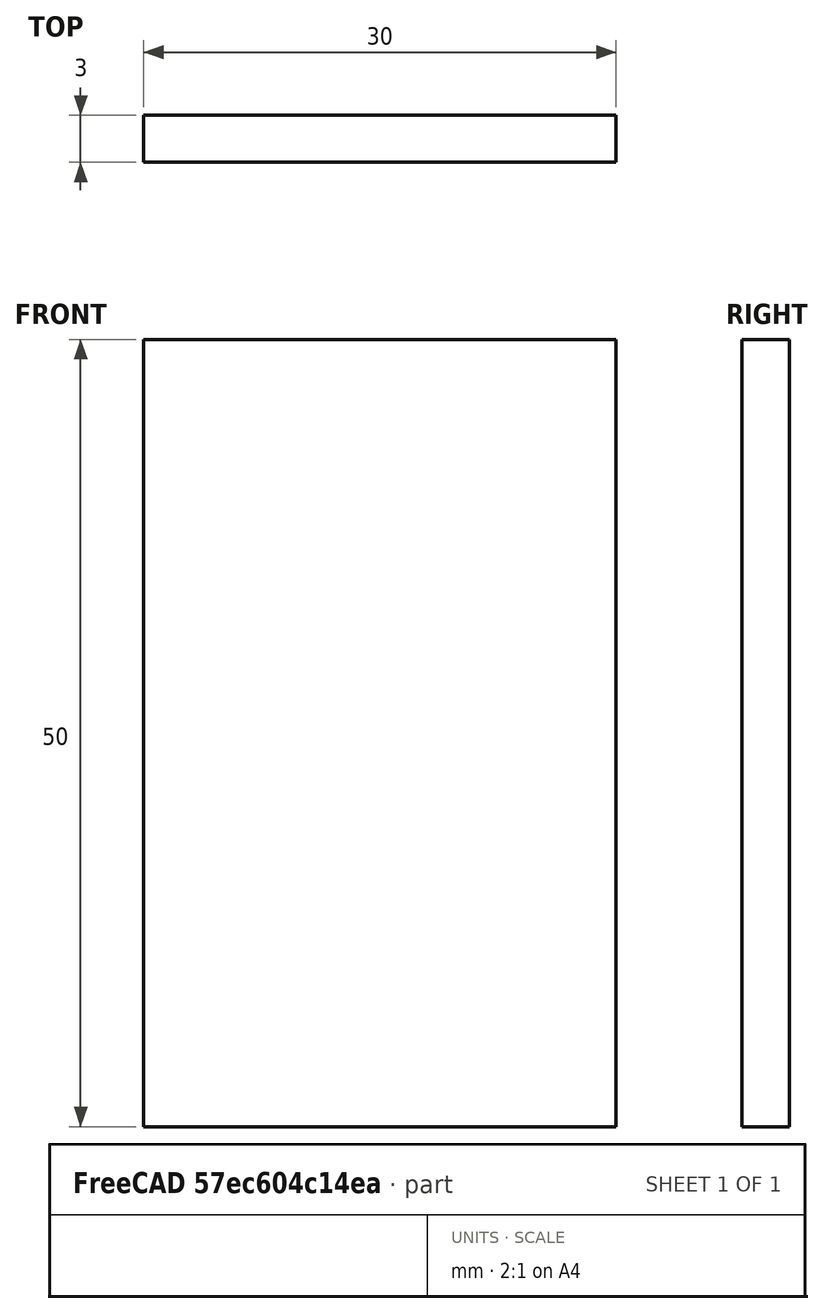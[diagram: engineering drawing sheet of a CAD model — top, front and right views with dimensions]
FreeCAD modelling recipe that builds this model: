
FCSTD DOCUMENT  (FreeCAD 0.15R4671 (Git))
Label: Flat Bar 30x3 EN10058 S235JR
License: All rights reserved
LicenseURL: http://en.wikipedia.org/wiki/All_rights_reserved
objects: Sketcher::SketchObject×1, Part::Extrusion×1
note: 2 computed .brp shape members not serialized (recipe doc carries the construction recipe); baked Part::Feature solids carry a one-line shape summary decoded from their .brp

FEATURE [Sketcher::SketchObject] Sketch
  sketch-geometry (4):
    g0: LineSegment StartX=-15 StartY=-1.5 StartZ=0 EndX=15 EndY=-1.5 EndZ=0
    g1: LineSegment StartX=15 StartY=-1.5 StartZ=0 EndX=15 EndY=1.5 EndZ=0
    g2: LineSegment StartX=15 StartY=1.5 StartZ=0 EndX=-15 EndY=1.5 EndZ=0
    g3: LineSegment StartX=-15 StartY=1.5 StartZ=0 EndX=-15 EndY=-1.5 EndZ=0
  constraints (12):
    c: Coincident(g0,g1)
    c: Coincident(g1,g2)
    c: Coincident(g2,g3)
    c: Coincident(g3,g0)
    c: Horizontal(g0)
    c: Horizontal(g2)
    c: Vertical(g1)
    c: Vertical(g3)
    c: Symmetric(g1,g2,g-2)
    c: Symmetric(g0,g1,g-1)
    c: DistanceY(g1) = 3
    c: DistanceX(g0) = 30
FEATURE [Part::Extrusion] Extrude  label="Flat Bar 30x3 EN10058 S235JR"
  Base = -> Sketch
  Dir = (0,0,50)
  Solid = true
